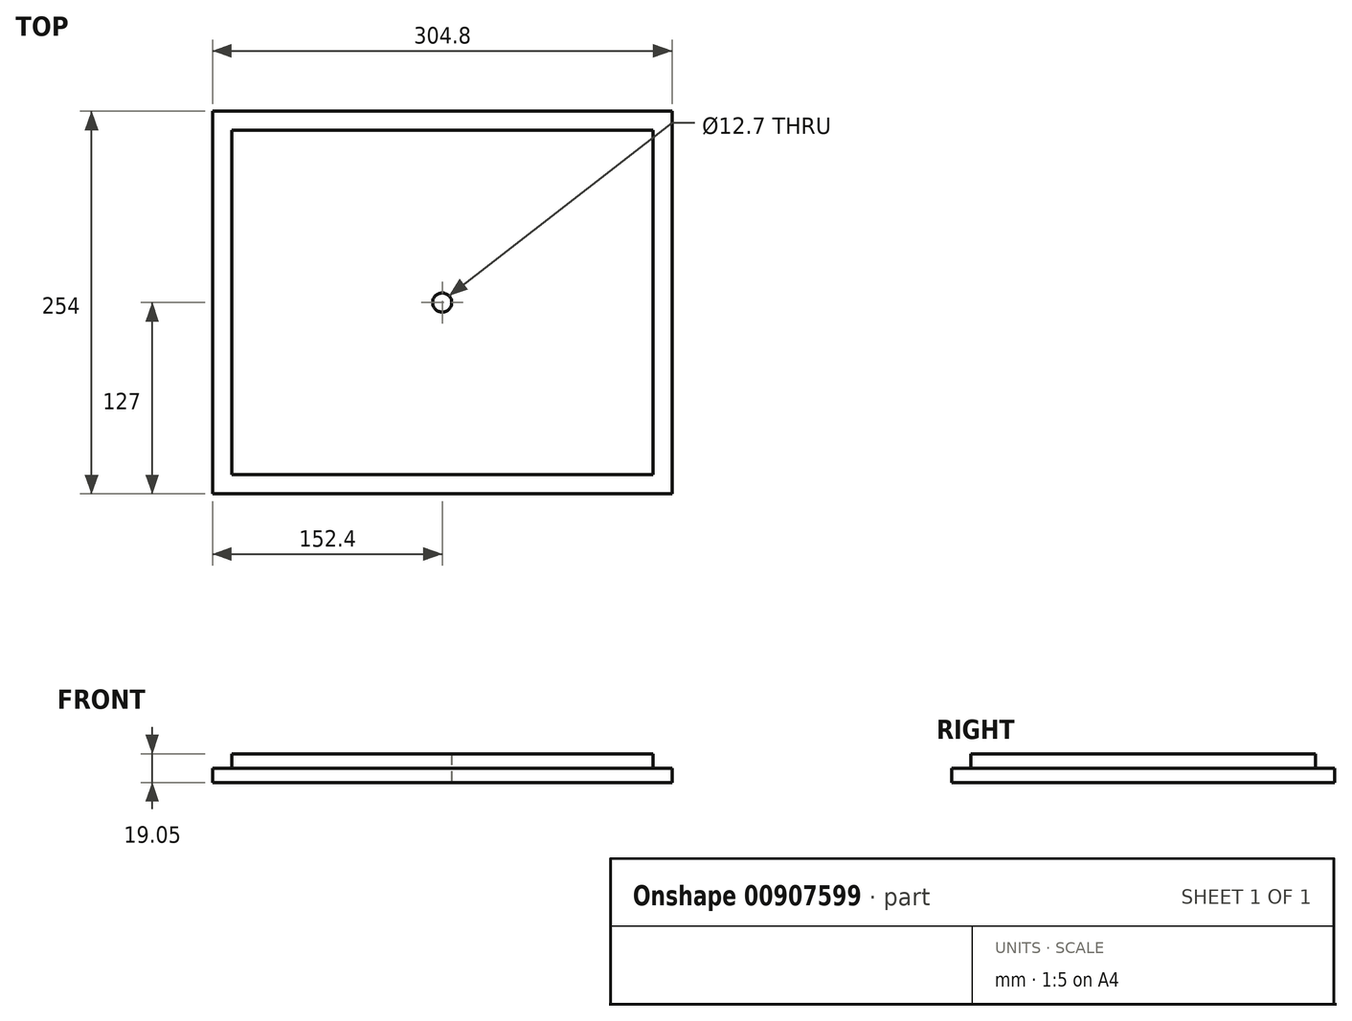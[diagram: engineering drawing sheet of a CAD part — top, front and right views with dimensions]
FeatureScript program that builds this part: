
annotation { "Feature Type Name" : "Feature", "Feature Type Description" : "" }
export const myFeature = defineFeature(function(context is Context, id is Id, definition is map)
    precondition{}
    {
        {
            var Q0;
            Q0=qCreatedBy(makeId("Top.planeOp"),FACE);
            var sketch = newSketch(context, id + "F0", { "sketchPlane" : qUnion([Q0])});
            skLineSegment(sketch, "E0.bottom", {"start": v(152.4, 127) * mm, "end": v(-152.4, 127) * mm});
            skLineSegment(sketch, "E0.top", {"start": v(152.4, -127) * mm, "end": v(-152.4, -127) * mm});
            skLineSegment(sketch, "E0.left", {"start": v(152.4, 127) * mm, "end": v(152.4, -127) * mm});
            skLineSegment(sketch, "E0.right", {"start": v(-152.4, 127) * mm, "end": v(-152.4, -127) * mm});
            skPoint(sketch, "E0.middle", {"position": v(0, 0) * mm});
            skSolve(sketch);
        }
        {
            var Q0;
            Q0=makeQuery(id+"F0.imprint","IMPRINT",FACE,{"disambiguationData":[TD([[makeQuery(id+"F0.imprint","IMPRINT",EDGE,{"derivedFrom":sQuery(id+"F0.wireOp",EDGE,"E0.bottom")}),1.0]])]});
            var sketch = newSketch(context, id + "F1", { "sketchPlane" : qUnion([Q0])});
            skLineSegment(sketch, "E1.bottom", {"start": v(139.7, 114.3) * mm, "end": v(-139.7, 114.3) * mm});
            skLineSegment(sketch, "E1.top", {"start": v(139.7, -114.3) * mm, "end": v(-139.7, -114.3) * mm});
            skLineSegment(sketch, "E1.left", {"start": v(139.7, 114.3) * mm, "end": v(139.7, -114.3) * mm});
            skLineSegment(sketch, "E1.right", {"start": v(-139.7, 114.3) * mm, "end": v(-139.7, -114.3) * mm});
            skPoint(sketch, "E1.middle", {"position": v(0, 0) * mm});
            skSolve(sketch);
        }
        {
            var Q0;
            Q0=makeQuery(id+"F1.imprint","IMPRINT",FACE,{"disambiguationData":[TD([[makeQuery(id+"F1.imprint","IMPRINT",EDGE,{"derivedFrom":sQuery(id+"F1.wireOp",EDGE,"E1.bottom")}),1.0]])]});
            var Q1;
            Q1=makeQuery(id+"F1.imprint","IMPRINT",FACE,{"disambiguationData":[TD([[makeQuery(id+"F1.imprint","IMPRINT",EDGE,{"derivedFrom":sQuery(id+"F1.wireOp",EDGE,"E1.bottom")}),-1.0]])]});
            extrude(context, id + "F2", {"entities" : qUnion([Q0, Q1]), "depth" : 9.52 * mm, "offsetDistance" : 25.4 * mm});
        }
        {
            var Q0;
            Q0=makeQuery(id+"F2.opExtrude","CAP_FACE",FACE,{"disambiguationData":[OSD([sQuery(id+"F0.wireOp",EDGE,"E0.bottom"),sQuery(id+"F0.wireOp",EDGE,"E0.top"),sQuery(id+"F0.wireOp",EDGE,"E0.left"),sQuery(id+"F0.wireOp",EDGE,"E0.right")])],"isStart":false});
            var sketch = newSketch(context, id + "F3", { "sketchPlane" : qUnion([Q0])});
            skLineSegment(sketch, "E2.bottom", {"start": v(139.7, 114.3) * mm, "end": v(-139.7, 114.3) * mm});
            skLineSegment(sketch, "E2.top", {"start": v(139.7, -114.3) * mm, "end": v(-139.7, -114.3) * mm});
            skLineSegment(sketch, "E2.left", {"start": v(139.7, 114.3) * mm, "end": v(139.7, -114.3) * mm});
            skLineSegment(sketch, "E2.right", {"start": v(-139.7, 114.3) * mm, "end": v(-139.7, -114.3) * mm});
            skPoint(sketch, "E2.middle", {"position": v(0, 0) * mm});
            skSolve(sketch);
        }
        {
            var Q0;
            Q0=makeQuery(id+"F3.imprint","IMPRINT",FACE,{"disambiguationData":[TD([[makeQuery(id+"F3.imprint","IMPRINT",EDGE,{"derivedFrom":sQuery(id+"F3.wireOp",EDGE,"E2.bottom")}),1.0]])]});
            extrude(context, id + "F4", {"entities" : qUnion([Q0]), "operationType" : NewBodyOperationType.ADD, "endBound" : BoundingType.SYMMETRIC, "depth" : 19.05 * mm, "offsetDistance" : 25.4 * mm});
        }
        {
            var Q0;
            Q0=makeQuery(id+"F4.opExtrude","CAP_FACE",FACE,{"disambiguationData":[OSD([sQuery(id+"F3.wireOp",EDGE,"E2.bottom"),sQuery(id+"F3.wireOp",EDGE,"E2.top"),sQuery(id+"F3.wireOp",EDGE,"E2.left"),sQuery(id+"F3.wireOp",EDGE,"E2.right")])],"isStart":false});
            var sketch = newSketch(context, id + "F5", { "sketchPlane" : qUnion([Q0])});
            skCircle(sketch, "E3", {"center": v(0, 0) * mm, "radius": 6.35 * mm});
            skSolve(sketch);
        }
        {
            var Q0;
            Q0 = qSketchRegion(id + "F5", true);
            extrude(context, id + "F6", {"entities" : qUnion([Q0]), "operationType" : NewBodyOperationType.REMOVE, "endBound" : BoundingType.SYMMETRIC, "oppositeDirection" : true, "depth" : 66.36 * mm, "offsetDistance" : 25.4 * mm});
        }
    });
